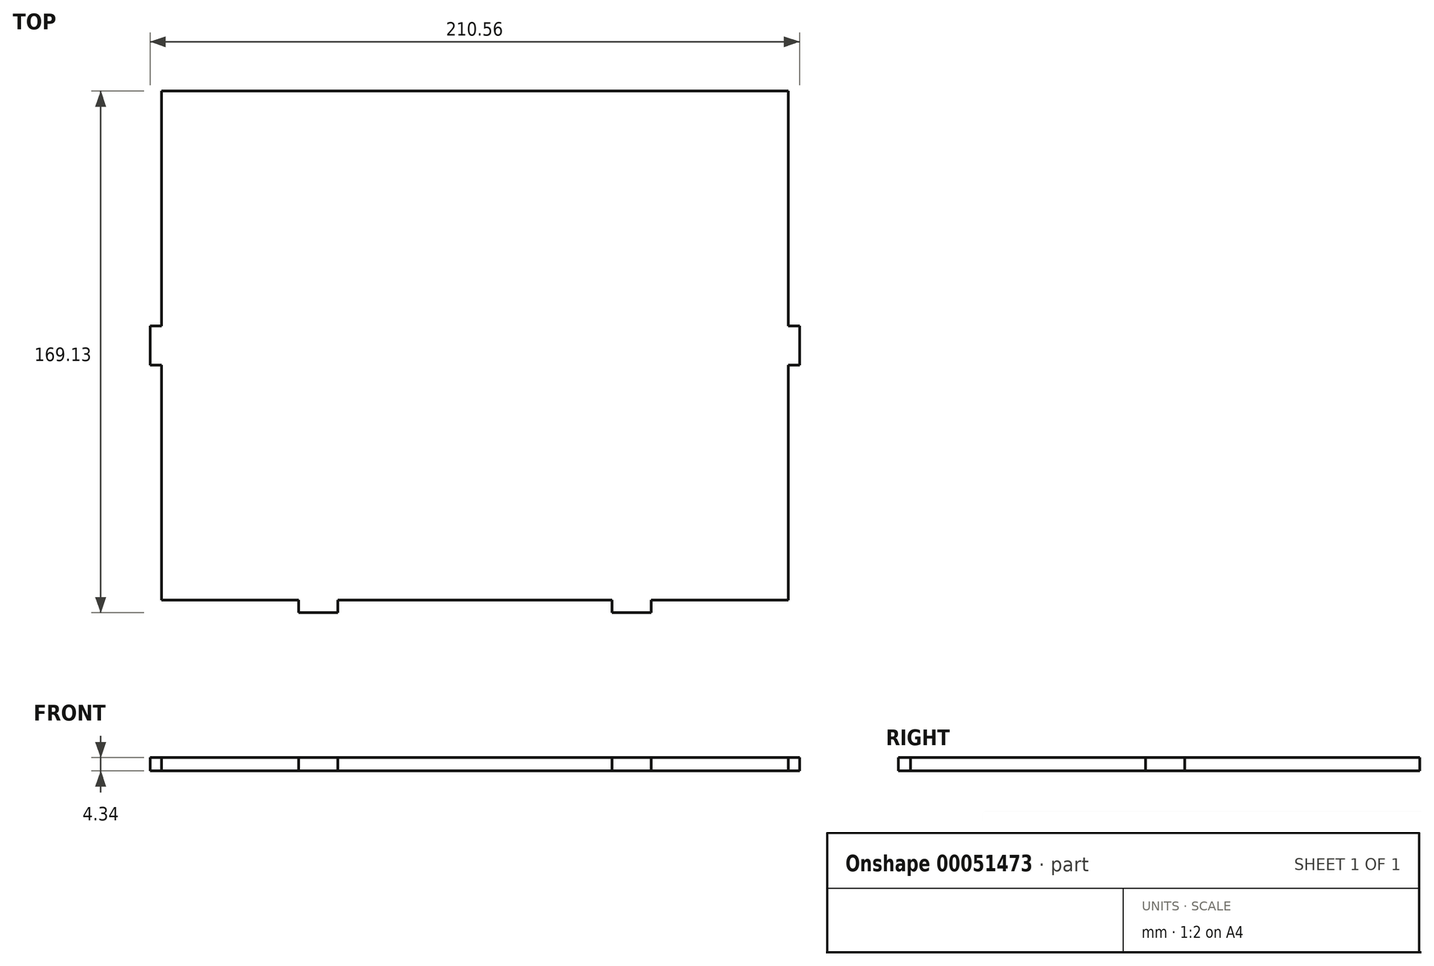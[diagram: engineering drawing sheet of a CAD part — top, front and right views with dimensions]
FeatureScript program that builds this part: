
annotation { "Feature Type Name" : "Feature", "Feature Type Description" : "" }
export const myFeature = defineFeature(function(context is Context, id is Id, definition is map)
    precondition{}
    {
        {
            var Q0;
            Q0=qCreatedBy(makeId("Top.planeOp"),FACE);
            var sketch = newSketch(context, id + "F0", { "sketchPlane" : qUnion([Q0])});
            skLineSegment(sketch, "E0.bottom", {"start": v(-55.6, 115.19) * mm, "end": v(147.6, 115.19) * mm});
            skLineSegment(sketch, "E0.top", {"start": v(-55.6, -49.91) * mm, "end": v(147.6, -49.91) * mm});
            skLineSegment(sketch, "E0.left", {"start": v(-55.6, 115.19) * mm, "end": v(-55.6, -49.91) * mm});
            skLineSegment(sketch, "E0.right", {"start": v(147.6, 115.19) * mm, "end": v(147.6, -49.91) * mm});
            skLineSegment(sketch, "E1", {"start": v(46, 115.19) * mm, "end": v(46, -49.91) * mm, "construction": true});
            skLineSegment(sketch, "E2.0", {"start": v(-4.8, 115.19) * mm, "end": v(-4.8, -49.91) * mm, "construction": true});
            skLineSegment(sketch, "E3.0", {"start": v(96.8, 115.19) * mm, "end": v(96.8, -49.91) * mm, "construction": true});
            skSolve(sketch);
        }
        {
            var Q0;
            Q0 = qSketchRegion(id + "F0", true);
            extrude(context, id + "F1", {"entities" : qUnion([Q0]), "oppositeDirection" : true, "depth" : 4.34 * mm});
        }
        {
            var Q0;
            Q0=qCreatedBy(makeId("Top.planeOp"),FACE);
            var sketch = newSketch(context, id + "F2", { "sketchPlane" : qUnion([Q0])});
            skLineSegment(sketch, "E4", {"start": v(-56.04, 115.28) * mm, "end": v(147.85, 115.28) * mm, "construction": true});
            skLineSegment(sketch, "E5", {"start": v(45.9, 115.28) * mm, "end": v(45.9, -75.25) * mm, "construction": true});
            skLineSegment(sketch, "E6.0", {"start": v(96.7, 115.28) * mm, "end": v(96.7, -49.51) * mm, "construction": true});
            skLineSegment(sketch, "E7.0", {"start": v(-4.9, 115.28) * mm, "end": v(-4.9, -49.6) * mm, "construction": true});
            skLineSegment(sketch, "E8", {"start": v(-11.25, -49.6) * mm, "end": v(-11.25, -53.94) * mm});
            skLineSegment(sketch, "E9", {"start": v(-11.25, -53.94) * mm, "end": v(-4.9, -53.94) * mm});
            skLineSegment(sketch, "E10", {"start": v(-11.25, -49.6) * mm, "end": v(-4.9, -49.6) * mm});
            skLineSegment(sketch, "E11.MirrorCS", {"start": v(103.05, -49.6) * mm, "end": v(103.05, -53.94) * mm});
            skLineSegment(sketch, "E12.MirrorCS", {"start": v(103.05, -49.6) * mm, "end": v(96.7, -49.6) * mm});
            skLineSegment(sketch, "E13.MirrorCS", {"start": v(103.05, -53.94) * mm, "end": v(96.7, -53.94) * mm});
            skPoint(sketch, "E14.MirrorCS.end.orphan", {"position": v(96.7, -49.6) * mm});
            skPoint(sketch, "E14.MirrorCS.start.orphan", {"position": v(96.7, -53.94) * mm});
            skLineSegment(sketch, "E15", {"start": v(-4.9, -49.6) * mm, "end": v(1.45, -49.6) * mm});
            skLineSegment(sketch, "E16", {"start": v(1.45, -49.6) * mm, "end": v(1.45, -53.94) * mm});
            skLineSegment(sketch, "E17", {"start": v(1.45, -53.94) * mm, "end": v(-4.9, -53.94) * mm});
            skLineSegment(sketch, "E18.MirrorCS", {"start": v(96.7, -49.6) * mm, "end": v(90.35, -49.6) * mm});
            skLineSegment(sketch, "E19.MirrorCS", {"start": v(90.35, -49.6) * mm, "end": v(90.35, -53.94) * mm});
            skLineSegment(sketch, "E20.MirrorCS", {"start": v(90.35, -53.94) * mm, "end": v(96.7, -53.94) * mm});
            skLineSegment(sketch, "E21", {"start": v(-55.76, 115.28) * mm, "end": v(-55.76, -49.72) * mm, "construction": true});
            skLineSegment(sketch, "E22", {"start": v(147.85, 115.28) * mm, "end": v(147.85, -49.29) * mm, "construction": true});
            skSolve(sketch);
        }
        {
            var Q0;
            Q0 = qSketchRegion(id + "F2", true);
            extrude(context, id + "F3", {"entities" : qUnion([Q0]), "operationType" : NewBodyOperationType.ADD, "oppositeDirection" : true, "depth" : 4.34 * mm});
        }
        {
            var Q0;
            Q0=qCreatedBy(makeId("Top.planeOp"),FACE);
            var sketch = newSketch(context, id + "F4", { "sketchPlane" : qUnion([Q0])});
            skLineSegment(sketch, "E23.0", {"start": v(-55.04, 38.99) * mm, "end": v(146.83, 38.99) * mm, "construction": true});
            skLineSegment(sketch, "E24.0", {"start": v(-55.04, 26.29) * mm, "end": v(146.83, 26.29) * mm, "construction": true});
            skLineSegment(sketch, "E25.bottom", {"start": v(-55.04, 26.29) * mm, "end": v(-59.39, 26.29) * mm});
            skLineSegment(sketch, "E25.top", {"start": v(-55.04, 38.99) * mm, "end": v(-59.39, 38.99) * mm});
            skLineSegment(sketch, "E25.left", {"start": v(-55.04, 26.29) * mm, "end": v(-55.04, 38.99) * mm});
            skLineSegment(sketch, "E25.right", {"start": v(-59.39, 26.29) * mm, "end": v(-59.39, 38.99) * mm});
            skLineSegment(sketch, "E26.bottom", {"start": v(146.83, 26.29) * mm, "end": v(151.17, 26.29) * mm});
            skLineSegment(sketch, "E26.top", {"start": v(146.83, 38.99) * mm, "end": v(151.17, 38.99) * mm});
            skLineSegment(sketch, "E26.left", {"start": v(146.83, 26.29) * mm, "end": v(146.83, 38.99) * mm});
            skLineSegment(sketch, "E26.right", {"start": v(151.17, 26.29) * mm, "end": v(151.17, 38.99) * mm});
            skLineSegment(sketch, "E27", {"start": v(45.9, -49.73) * mm, "end": v(45.9, 114.99) * mm, "construction": true});
            skPoint(sketch, "E27.startSnap0", {"position": v(45.9, 38.99) * mm});
            skSolve(sketch);
        }
        {
            var Q0;
            Q0 = qSketchRegion(id + "F4", true);
            extrude(context, id + "F5", {"entities" : qUnion([Q0]), "operationType" : NewBodyOperationType.ADD, "oppositeDirection" : true, "depth" : 4.34 * mm});
        }
    });
